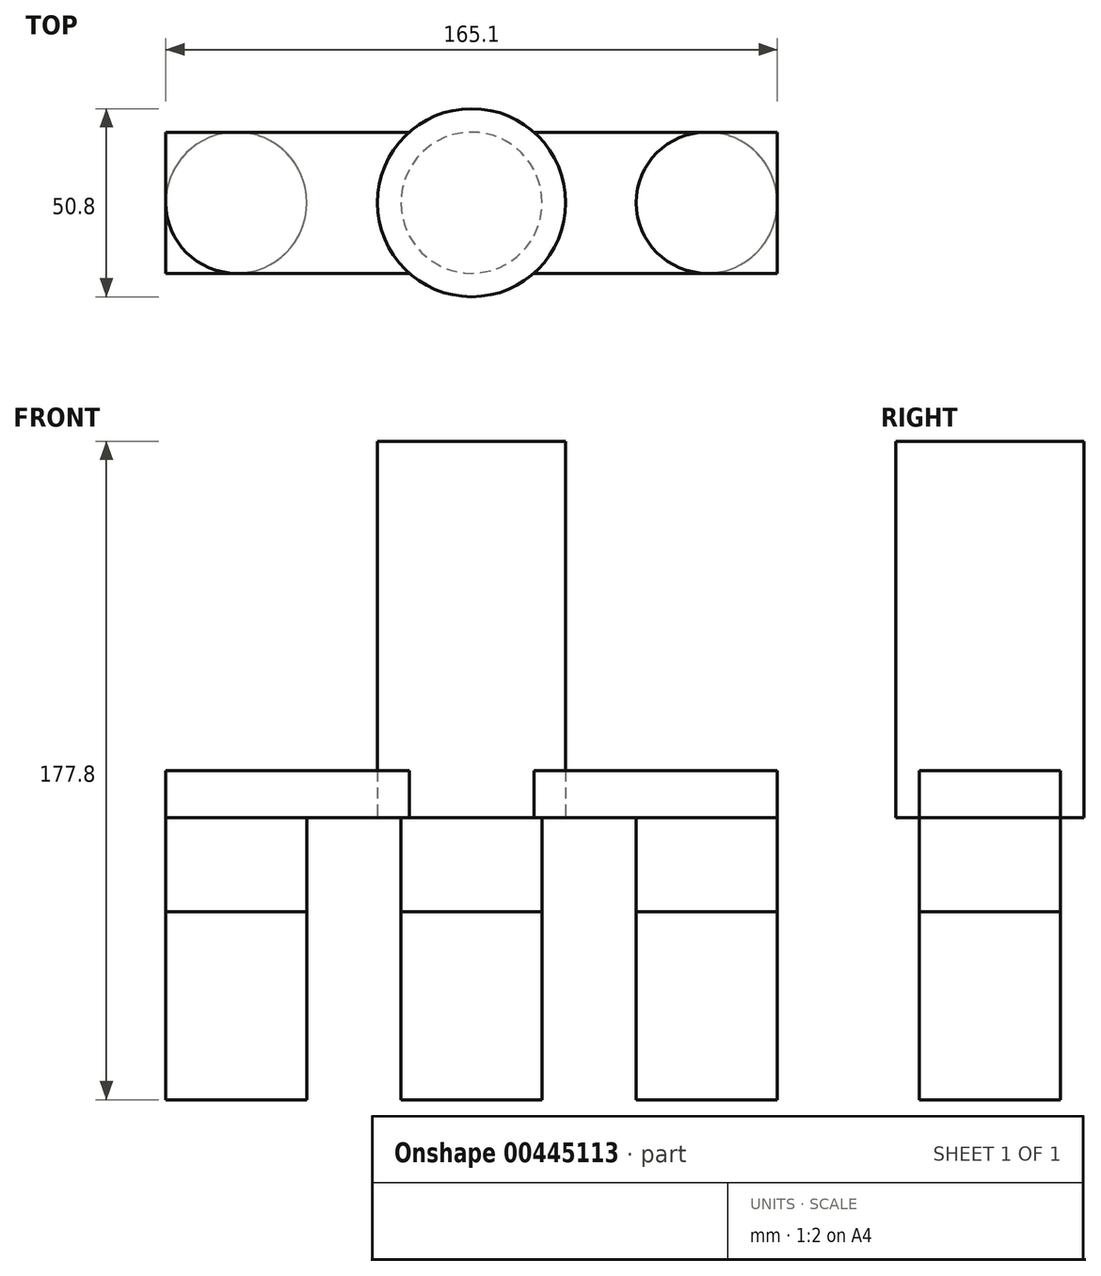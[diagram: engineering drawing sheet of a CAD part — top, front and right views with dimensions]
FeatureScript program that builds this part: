
annotation { "Feature Type Name" : "Feature", "Feature Type Description" : "" }
export const myFeature = defineFeature(function(context is Context, id is Id, definition is map)
    precondition{}
    {
        {
            var Q0;
            Q0=qCreatedBy(makeId("Top.planeOp"),FACE);
            var sketch = newSketch(context, id + "F0", { "sketchPlane" : qUnion([Q0])});
            skCircle(sketch, "E0", {"center": v(0, 0) * mm, "radius": 25.4 * mm});
            skLineSegment(sketch, "E1.bottom", {"start": v(82.55, 19.05) * mm, "end": v(-82.55, 19.05) * mm});
            skLineSegment(sketch, "E1.top", {"start": v(82.55, -19.05) * mm, "end": v(-82.55, -19.05) * mm});
            skLineSegment(sketch, "E1.left", {"start": v(82.55, 19.05) * mm, "end": v(82.55, -19.05) * mm});
            skLineSegment(sketch, "E1.right", {"start": v(-82.55, 19.05) * mm, "end": v(-82.55, -19.05) * mm});
            skSolve(sketch);
        }
        {
            var Q0;
            {var subQ5=sQuery(id+"F0.wireOp",EDGE,"E1.right");Q0=makeQuery(id+"F0.imprint","IMPRINT",FACE,{"disambiguationData":[TD([[makeQuery(id+"F0.imprint","IMPRINT",EDGE,{"derivedFrom":subQ5}),1.0]])]});}
            var Q1;
            {var subQ5=sQuery(id+"F0.wireOp",EDGE,"E1.left");Q1=makeQuery(id+"F0.imprint","IMPRINT",FACE,{"disambiguationData":[TD([[makeQuery(id+"F0.imprint","IMPRINT",EDGE,{"derivedFrom":subQ5}),-1.0]])]});}
            extrude(context, id + "F1", {"entities" : qUnion([Q0, Q1]), "depth" : 12.7 * mm});
        }
        {
            var Q0;
            {var subQ0=sQuery(id+"F0.wireOp",EDGE,"E1.bottom");var subQ1=sQuery(id+"F0.wireOp",EDGE,"E0");var subQ2=makeQuery(id+"F0.imprint","INTERSECT",VERTEX,{"disambiguationData":[OD(0.0)],"derivedFrom":[subQ1,subQ0]});Q0=makeQuery(id+"F0.imprint","IMPRINT",FACE,{"disambiguationData":[TD([[makeQuery(id+"F0.imprint","IMPRINT",EDGE,{"disambiguationData":[TD([[subQ2,1.0]])],"derivedFrom":subQ1}),1.0]])]});}
            var Q1;
            {var subQ0=sQuery(id+"F0.wireOp",EDGE,"E1.top");var subQ1=sQuery(id+"F0.wireOp",EDGE,"E0");var subQ2=makeQuery(id+"F0.imprint","INTERSECT",VERTEX,{"disambiguationData":[OD(0.0)],"derivedFrom":[subQ1,subQ0]});Q1=makeQuery(id+"F0.imprint","IMPRINT",FACE,{"disambiguationData":[TD([[makeQuery(id+"F0.imprint","IMPRINT",EDGE,{"disambiguationData":[TD([[subQ2,-1.0]])],"derivedFrom":subQ1}),1.0]])]});}
            var Q2;
            {var subQ0=sQuery(id+"F0.wireOp",EDGE,"E1.bottom");var subQ1=sQuery(id+"F0.wireOp",EDGE,"E0");var subQ2=makeQuery(id+"F0.imprint","INTERSECT",VERTEX,{"disambiguationData":[OD(0.0)],"derivedFrom":[subQ1,subQ0]});Q2=makeQuery(id+"F0.imprint","IMPRINT",FACE,{"disambiguationData":[TD([[makeQuery(id+"F0.imprint","IMPRINT",EDGE,{"disambiguationData":[TD([[subQ2,-1.0]])],"derivedFrom":subQ1}),1.0]])]});}
            extrude(context, id + "F2", {"entities" : qUnion([Q0, Q1, Q2]), "depth" : 101.6 * mm});
        }
        {
            var Q0;
            Q0=makeQuery(id+"F1.opExtrude","CAP_FACE",FACE,{"disambiguationData":[OSD([sQuery(id+"F0.wireOp",EDGE,"E0"),sQuery(id+"F0.wireOp",EDGE,"E1.bottom"),sQuery(id+"F0.wireOp",EDGE,"E1.top"),sQuery(id+"F0.wireOp",EDGE,"E1.left")])],"isStart":true});
            var sketch = newSketch(context, id + "F3", { "sketchPlane" : qUnion([Q0])});
            skCircle(sketch, "E2", {"center": v(0, 0) * mm, "radius": 19.05 * mm});
            skLineSegment(sketch, "E3", {"start": v(-19.05, 0) * mm, "end": v(-63.5, 0) * mm});
            skCircle(sketch, "E4", {"center": v(-63.5, 0) * mm, "radius": 19.05 * mm});
            skLineSegment(sketch, "E5", {"start": v(19.05, 0) * mm, "end": v(63.5, 0) * mm});
            skPoint(sketch, "E5.endSnap0", {"position": v(25.4, 0) * mm});
            skCircle(sketch, "E6", {"center": v(63.5, 0) * mm, "radius": 19.05 * mm});
            skSolve(sketch);
        }
        {
            var Q0;
            Q0 = qSketchRegion(id + "F3", true);
            extrude(context, id + "F4", {"entities" : qUnion([Q0]), "depth" : 25.4 * mm});
        }
        {
            var Q0;
            Q0 = qSketchRegion(id + "F3", true);
            extrude(context, id + "F5", {"entities" : qUnion([Q0]), "depth" : 76.2 * mm});
        }
    });
